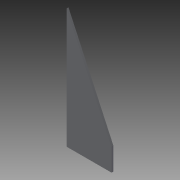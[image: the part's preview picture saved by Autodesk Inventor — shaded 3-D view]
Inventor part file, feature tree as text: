
AUTODESK INVENTOR PART (.ipt)
format: ipt  version: 2013 (Build 170138000, 138)  size: 66,048 bytes
history: native  units: in
note: dims shown in document units (in); Inventor stores cm internally (conversion verified against a paired STEP export)
features: extrude x1, sketch x1
ambient origin geometry x8: Origin, YZ Plane, XZ Plane, XY Plane, X Axis, Y Axis, Z Axis, Center Point
bodies: Solid1 (feature_tree)
feature tree (2):
  extrude  "Extrusion1"  Depth=1.5in
  sketch  "Sketch1"  dims[d0=3.0in d1=1.5in d2=8.0in d3=0.125in d4=0.0in]
